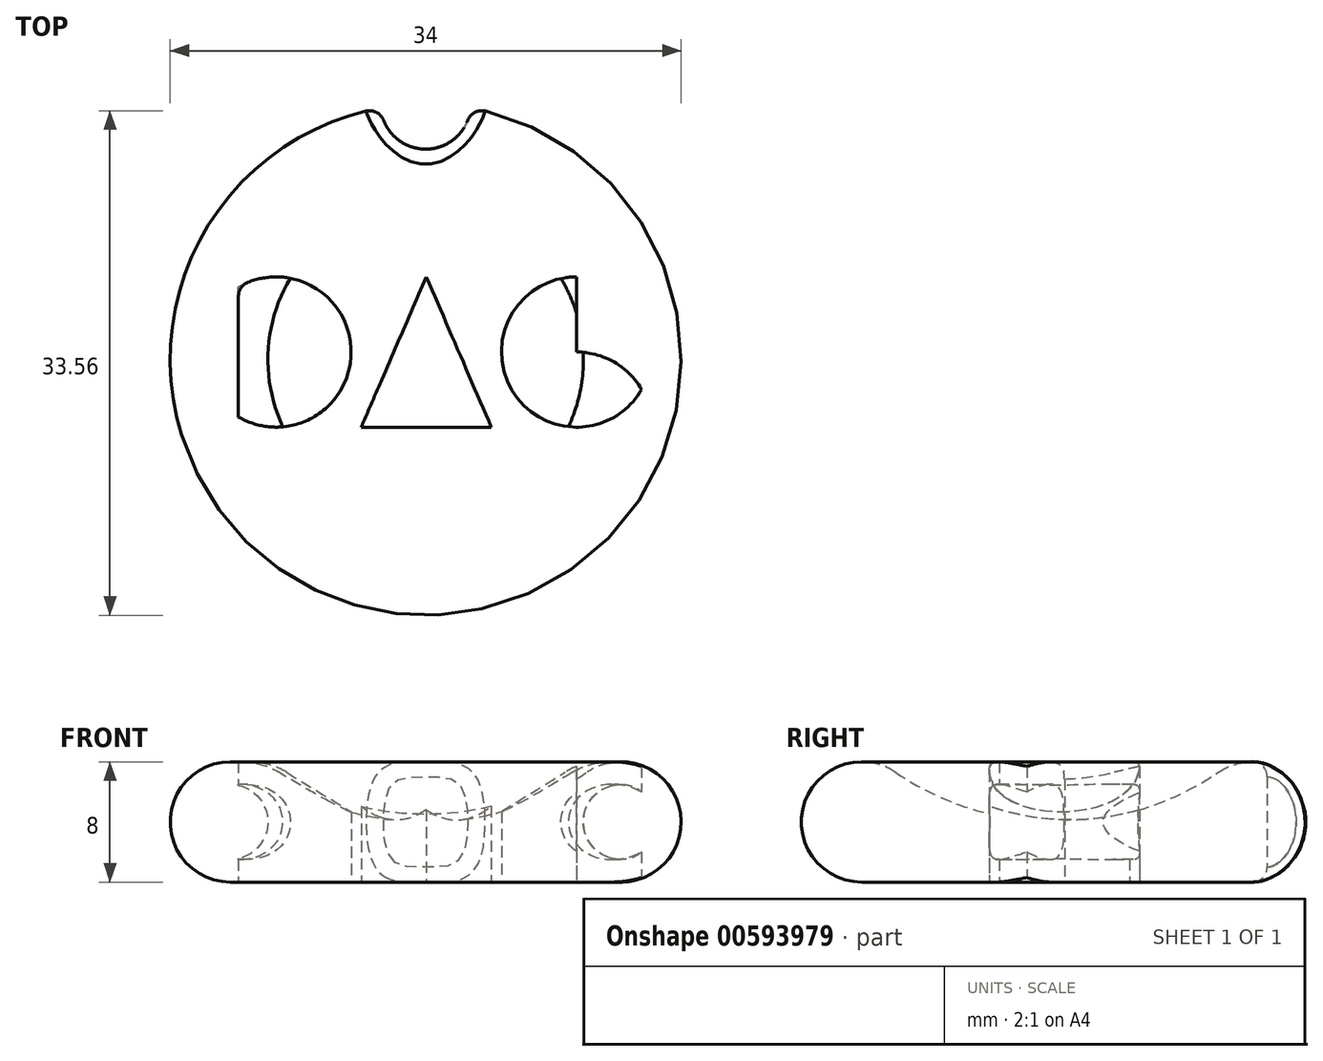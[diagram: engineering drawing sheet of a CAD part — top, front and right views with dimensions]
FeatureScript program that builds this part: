
annotation { "Feature Type Name" : "Feature", "Feature Type Description" : "" }
export const myFeature = defineFeature(function(context is Context, id is Id, definition is map)
    precondition{}
    {
        {
            var Q0;
            Q0=qCreatedBy(makeId("Front.planeOp"),FACE);
            var sketch = newSketch(context, id + "F0", { "sketchPlane" : qUnion([Q0])});
            skArc(sketch, "E0", {"start": v(-10.75, 7.3) * mm, "mid": v(-5.62, 4.85) * mm, "end": v(0, 4) * mm});
            skArc(sketch, "E1", {"start": v(-10.75, 7.3) * mm, "mid": v(-16.82, 5.18) * mm, "end": v(-13, 0) * mm});
            skLineSegment(sketch, "E2", {"start": v(0, 0) * mm, "end": v(-13, 0) * mm});
            skLineSegment(sketch, "E3", {"start": v(-13, 0) * mm, "end": v(0, 0) * mm});
            skLineSegment(sketch, "E4", {"start": v(0, 0) * mm, "end": v(0, 23.13) * mm});
            skLineSegment(sketch, "E5", {"start": v(-17, 0) * mm, "end": v(-17, 29.65) * mm});
            skSolve(sketch);
        }
        {
            var Q0;
            {var subQ0=sQuery(id+"F0.wireOp",EDGE,"E0");Q0=makeQuery(id+"F0.imprint","IMPRINT",FACE,{"disambiguationData":[TD([[makeQuery(id+"F0.imprint","IMPRINT",EDGE,{"derivedFrom":subQ0}),-1.0]])]});}
            var Q1;
            Q1=sQuery(id+"F0.wireOp",EDGE,"E4");
            revolve(context, id + "F1", {"entities" : qUnion([Q0]), "axis" : qUnion([Q1]), "revolveType" : RevolveType.FULL});
        }
        {
            var Q0;
            Q0=qCreatedBy(makeId("Top.planeOp"),FACE);
            var sketch = newSketch(context, id + "F2", { "sketchPlane" : qUnion([Q0])});
            skArc(sketch, "E6", {"start": v(-12.46, -3.82) * mm, "mid": v(-4.96, 0.5) * mm, "end": v(-12.46, 4.84) * mm});
            skArc(sketch, "E7", {"start": v(10.04, 5.5) * mm, "mid": v(5.71, -2) * mm, "end": v(14.37, -2) * mm});
            skLineSegment(sketch, "E8", {"start": v(-12.46, -3.82) * mm, "end": v(-12.46, 4.84) * mm});
            skLineSegment(sketch, "E9", {"start": v(0.04, -4.5) * mm, "end": v(4.37, -4.5) * mm});
            skLineSegment(sketch, "E10", {"start": v(0.04, -4.5) * mm, "end": v(-4.29, -4.5) * mm});
            skLineSegment(sketch, "E11", {"start": v(-4.29, -4.5) * mm, "end": v(0.04, 5.5) * mm});
            skLineSegment(sketch, "E12", {"start": v(4.37, -4.5) * mm, "end": v(0.04, 5.5) * mm});
            skLineSegment(sketch, "E13", {"start": v(10.04, 5.5) * mm, "end": v(10.04, -4.5) * mm});
            skArc(sketch, "E14", {"start": v(14.37, -2) * mm, "mid": v(10.04, 0.5) * mm, "end": v(5.71, -2) * mm});
            skSolve(sketch);
        }
        {
            var Q0;
            Q0 = qSketchRegion(id + "F2", true);
            extrude(context, id + "F3", {"entities" : qUnion([Q0]), "operationType" : NewBodyOperationType.REMOVE, "depth" : 21.5 * mm, "offsetDistance" : 25 * mm});
        }
        {
            var Q0;
            Q0=qCreatedBy(makeId("Front.planeOp"),FACE);
            var sketch = newSketch(context, id + "F4", { "sketchPlane" : qUnion([Q0])});
            skCircle(sketch, "E15", {"center": v(-13, 4) * mm, "radius": 2.5 * mm});
            skLineSegment(sketch, "E16", {"start": v(0, 0) * mm, "end": v(0, 5.66) * mm});
            skSolve(sketch);
        }
        {
            var Q0;
            Q0 = qSketchRegion(id + "F4", true);
            var Q1;
            Q1=sQuery(id+"F4.wireOp",EDGE,"E16");
            revolve(context, id + "F5", {"operationType" : NewBodyOperationType.ADD, "entities" : qUnion([Q0]), "axis" : qUnion([Q1]), "revolveType" : RevolveType.FULL});
        }
        {
            var Q0;
            Q0=qCreatedBy(makeId("Top.planeOp"),FACE);
            var sketch = newSketch(context, id + "F6", { "sketchPlane" : qUnion([Q0])});
            skCircle(sketch, "E17", {"center": v(0, 17) * mm, "radius": 3 * mm});
            skSolve(sketch);
        }
        {
            var Q0;
            Q0 = qSketchRegion(id + "F6", true);
            extrude(context, id + "F7", {"entities" : qUnion([Q0]), "operationType" : NewBodyOperationType.REMOVE, "depth" : 25 * mm, "offsetDistance" : 25 * mm});
        }
        {
            var Q0;
            Q0=makeQuery(id+"F7.boolean.opBoolean","INTERSECT",EDGE,{"derivedFrom":[makeQuery(id+"F1.opRevolve","SWEPT_FACE",FACE,{"disambiguationData":[OSD([sQuery(id+"F0.wireOp",EDGE,"E1")])]}),makeQuery(id+"F7.opExtrude","SWEPT_FACE",FACE,{"disambiguationData":[OSD([sQuery(id+"F6.wireOp",EDGE,"E17")])]})]});
            fillet(context, id + "F8", {"entities" : qUnion([Q0]), "radius" : 1 * mm, "tangentPropagation" : true, "allowEdgeOverflow" : false});
        }
        {
            var Q0;
            {var subQ0=sQuery(id+"F2.wireOp",EDGE,"E8");var subQ1=sQuery(id+"F2.wireOp",EDGE,"E6");Q0=makeQuery(id+"F5.boolean.opBoolean","SPLIT",EDGE,{"disambiguationData":[OD(1.0)],"derivedFrom":makeQuery(id+"F3.boolean.opBoolean","COPY",EDGE,{"derivedFrom":makeQuery(id+"F3.opExtrude","SWEPT_EDGE",EDGE,{"disambiguationData":[OSD([subQ1,subQ0]),TDD([makeQuery(id+"F2.imprint","INTERSECT",VERTEX,{"disambiguationData":[OD(1.0)],"derivedFrom":[subQ1,subQ0]})])]})})});}
            fillet(context, id + "F9", {"entities" : qUnion([Q0]), "radius" : 1 * mm, "tangentPropagation" : true, "allowEdgeOverflow" : false});
        }
    });
